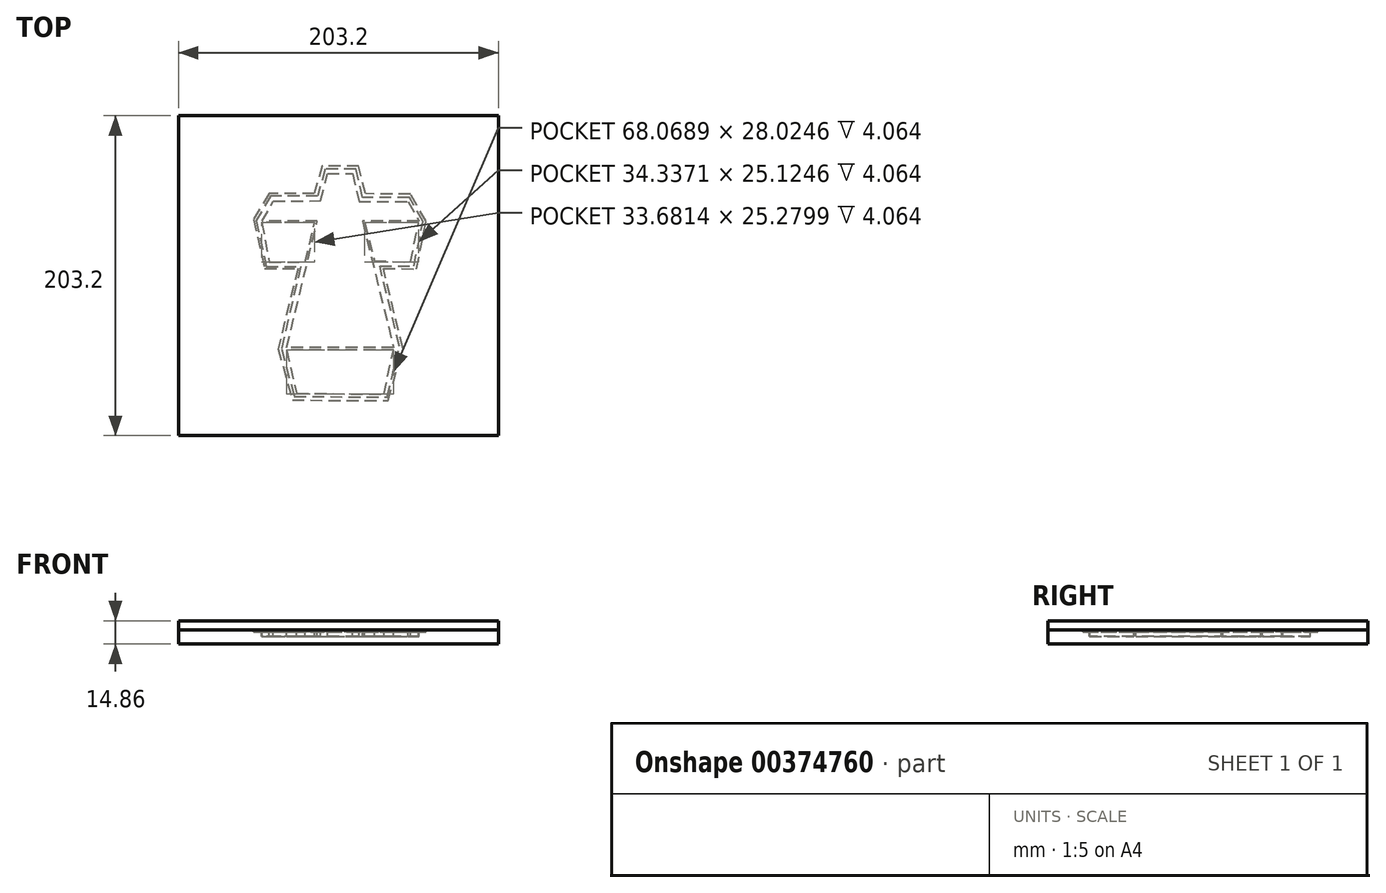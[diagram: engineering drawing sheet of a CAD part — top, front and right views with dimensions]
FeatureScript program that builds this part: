
annotation { "Feature Type Name" : "Feature", "Feature Type Description" : "" }
export const myFeature = defineFeature(function(context is Context, id is Id, definition is map)
    precondition{}
    {
        {
            var Q0;
            Q0=qCreatedBy(makeId("Top.planeOp"),FACE);
            var sketch = newSketch(context, id + "F0", { "sketchPlane" : qUnion([Q0])});
            skLineSegment(sketch, "E0.bottom", {"start": v(0, 0) * mm, "end": v(101.6, 0) * mm});
            skLineSegment(sketch, "E0.top", {"start": v(0, 101.6) * mm, "end": v(101.6, 101.6) * mm});
            skLineSegment(sketch, "E0.left", {"start": v(0, 0) * mm, "end": v(0, 101.6) * mm});
            skLineSegment(sketch, "E0.right", {"start": v(101.6, 0) * mm, "end": v(101.6, 101.6) * mm});
            skSolve(sketch);
        }
        {
            var Q0;
            Q0 = qSketchRegion(id + "F0", true);
            extrude(context, id + "F1", {"entities" : qUnion([Q0]), "depth" : 4.44 * mm});
        }
        {
            var Q0;
            Q0=qCreatedBy(makeId("Top.planeOp"),FACE);
            var sketch = newSketch(context, id + "F2", { "sketchPlane" : qUnion([Q0])});
            skLineSegment(sketch, "E1", {"start": v(33.3, 27.25) * mm, "end": v(67.33, 27.25) * mm});
            skLineSegment(sketch, "E2", {"start": v(67.33, 27.25) * mm, "end": v(64.05, 13.42) * mm});
            skLineSegment(sketch, "E3", {"start": v(64.05, 13.42) * mm, "end": v(36.34, 13.24) * mm});
            skLineSegment(sketch, "E4", {"start": v(36.34, 13.24) * mm, "end": v(33.3, 27.25) * mm});
            skLineSegment(sketch, "E5", {"start": v(33.27, 27.95) * mm, "end": v(67.18, 27.95) * mm});
            skLineSegment(sketch, "E6", {"start": v(67.18, 27.95) * mm, "end": v(57.5, 68.13) * mm});
            skLineSegment(sketch, "E7", {"start": v(57.5, 68.13) * mm, "end": v(74.96, 68.13) * mm});
            skLineSegment(sketch, "E8", {"start": v(74.96, 68.13) * mm, "end": v(71.49, 74.45) * mm});
            skLineSegment(sketch, "E9", {"start": v(71.49, 74.45) * mm, "end": v(56.48, 74.61) * mm});
            skLineSegment(sketch, "E10", {"start": v(56.48, 74.61) * mm, "end": v(54.27, 83.33) * mm});
            skLineSegment(sketch, "E11", {"start": v(54.27, 83.33) * mm, "end": v(46.3, 83.33) * mm});
            skLineSegment(sketch, "E12", {"start": v(46.3, 83.33) * mm, "end": v(44.3, 74.4) * mm});
            skLineSegment(sketch, "E13", {"start": v(44.3, 74.4) * mm, "end": v(28.63, 74.35) * mm});
            skLineSegment(sketch, "E14", {"start": v(28.63, 74.35) * mm, "end": v(25.18, 68.15) * mm});
            skLineSegment(sketch, "E15", {"start": v(25.18, 68.15) * mm, "end": v(43.15, 68.15) * mm});
            skLineSegment(sketch, "E16", {"start": v(43.15, 68.15) * mm, "end": v(33.27, 27.95) * mm});
            skLineSegment(sketch, "E17", {"start": v(27.84, 55.17) * mm, "end": v(25.3, 67.74) * mm});
            skLineSegment(sketch, "E18", {"start": v(25.3, 67.74) * mm, "end": v(42.46, 67.74) * mm});
            skLineSegment(sketch, "E19", {"start": v(42.46, 67.74) * mm, "end": v(39.37, 55.52) * mm});
            skLineSegment(sketch, "E20", {"start": v(39.37, 55.52) * mm, "end": v(27.84, 55.17) * mm});
            skLineSegment(sketch, "E21", {"start": v(61.35, 55.14) * mm, "end": v(58.33, 67.72) * mm});
            skLineSegment(sketch, "E22", {"start": v(58.33, 67.72) * mm, "end": v(75.17, 67.78) * mm});
            skLineSegment(sketch, "E23", {"start": v(75.17, 67.78) * mm, "end": v(72.74, 55.17) * mm});
            skLineSegment(sketch, "E24", {"start": v(72.74, 55.17) * mm, "end": v(61.35, 55.14) * mm});
            skLineSegment(sketch, "E25", {"start": v(31.23, 27.83) * mm, "end": v(37.63, 53.87) * mm});
            skLineSegment(sketch, "E26", {"start": v(37.63, 53.87) * mm, "end": v(26.8, 53.87) * mm});
            skLineSegment(sketch, "E27", {"start": v(26.8, 53.87) * mm, "end": v(23.84, 67.92) * mm});
            skLineSegment(sketch, "E28", {"start": v(23.84, 67.92) * mm, "end": v(28.27, 75.64) * mm});
            skLineSegment(sketch, "E29", {"start": v(28.27, 75.64) * mm, "end": v(43.14, 75.64) * mm});
            skLineSegment(sketch, "E30", {"start": v(43.14, 75.64) * mm, "end": v(45.18, 84.73) * mm});
            skLineSegment(sketch, "E31", {"start": v(45.18, 84.73) * mm, "end": v(55.09, 84.73) * mm});
            skLineSegment(sketch, "E32", {"start": v(55.09, 84.73) * mm, "end": v(57.37, 76.07) * mm});
            skLineSegment(sketch, "E33", {"start": v(57.37, 76.07) * mm, "end": v(72.25, 76.07) * mm});
            skLineSegment(sketch, "E34", {"start": v(72.25, 76.07) * mm, "end": v(76.93, 68.32) * mm});
            skLineSegment(sketch, "E35", {"start": v(76.93, 68.32) * mm, "end": v(73.68, 53.8) * mm});
            skLineSegment(sketch, "E36", {"start": v(73.68, 53.8) * mm, "end": v(62.8, 53.78) * mm});
            skLineSegment(sketch, "E37", {"start": v(62.8, 53.78) * mm, "end": v(68.9, 27.55) * mm});
            skLineSegment(sketch, "E38", {"start": v(68.9, 27.55) * mm, "end": v(64.68, 12.02) * mm});
            skLineSegment(sketch, "E39", {"start": v(64.68, 12.02) * mm, "end": v(35.19, 11.83) * mm});
            skLineSegment(sketch, "E40", {"start": v(35.19, 11.83) * mm, "end": v(31.23, 27.83) * mm});
            skLineSegment(sketch, "E41", {"start": v(34.82, 11.04) * mm, "end": v(30.12, 27.76) * mm});
            skLineSegment(sketch, "E42", {"start": v(30.12, 27.76) * mm, "end": v(36.13, 52.85) * mm});
            skLineSegment(sketch, "E43", {"start": v(36.13, 52.85) * mm, "end": v(25.99, 52.78) * mm});
            skLineSegment(sketch, "E44", {"start": v(25.99, 52.78) * mm, "end": v(22.75, 67.97) * mm});
            skLineSegment(sketch, "E45", {"start": v(22.75, 67.97) * mm, "end": v(27.91, 76.74) * mm});
            skLineSegment(sketch, "E46", {"start": v(27.91, 76.74) * mm, "end": v(42.38, 76.84) * mm});
            skLineSegment(sketch, "E47", {"start": v(42.38, 76.84) * mm, "end": v(44.37, 85.7) * mm});
            skLineSegment(sketch, "E48", {"start": v(44.37, 85.7) * mm, "end": v(55.99, 85.7) * mm});
            skLineSegment(sketch, "E49", {"start": v(55.99, 85.7) * mm, "end": v(58.47, 76.89) * mm});
            skLineSegment(sketch, "E50", {"start": v(58.47, 76.89) * mm, "end": v(72.85, 76.98) * mm});
            skLineSegment(sketch, "E51", {"start": v(72.85, 76.98) * mm, "end": v(77.76, 68.69) * mm});
            skLineSegment(sketch, "E52", {"start": v(77.76, 68.69) * mm, "end": v(74.25, 53.04) * mm});
            skLineSegment(sketch, "E53", {"start": v(74.25, 53.04) * mm, "end": v(63.89, 53.04) * mm});
            skLineSegment(sketch, "E54", {"start": v(63.89, 53.04) * mm, "end": v(69.95, 28.5) * mm});
            skLineSegment(sketch, "E55", {"start": v(69.95, 28.5) * mm, "end": v(65.02, 11.23) * mm});
            skLineSegment(sketch, "E56", {"start": v(65.02, 11.23) * mm, "end": v(34.82, 11.04) * mm});
            skSolve(sketch);
        }
        {
            var Q0;
            Q0=qCreatedBy(makeId("Top.planeOp"),FACE);
            var sketch = newSketch(context, id + "F3", { "sketchPlane" : qUnion([Q0])});
            skLineSegment(sketch, "E57", {"start": v(31.37, 28.38) * mm, "end": v(37.63, 53.87) * mm});
            skLineSegment(sketch, "E58", {"start": v(37.63, 53.87) * mm, "end": v(26.8, 53.87) * mm});
            skLineSegment(sketch, "E59", {"start": v(26.8, 53.87) * mm, "end": v(23.97, 68.09) * mm});
            skLineSegment(sketch, "E60", {"start": v(23.97, 68.09) * mm, "end": v(28.27, 75.64) * mm});
            skLineSegment(sketch, "E61", {"start": v(28.27, 75.64) * mm, "end": v(43.14, 75.64) * mm});
            skLineSegment(sketch, "E62", {"start": v(43.14, 75.64) * mm, "end": v(45.18, 84.73) * mm});
            skLineSegment(sketch, "E63", {"start": v(45.18, 84.73) * mm, "end": v(55.09, 84.73) * mm});
            skLineSegment(sketch, "E64", {"start": v(55.09, 84.73) * mm, "end": v(57.37, 76.07) * mm});
            skLineSegment(sketch, "E65", {"start": v(57.37, 76.07) * mm, "end": v(72.25, 76.07) * mm});
            skLineSegment(sketch, "E66", {"start": v(72.25, 76.07) * mm, "end": v(76.93, 68.32) * mm});
            skLineSegment(sketch, "E67", {"start": v(76.93, 68.32) * mm, "end": v(73.68, 53.8) * mm});
            skLineSegment(sketch, "E68", {"start": v(73.68, 53.8) * mm, "end": v(62.8, 53.78) * mm});
            skLineSegment(sketch, "E69", {"start": v(62.8, 53.78) * mm, "end": v(68.9, 27.55) * mm});
            skLineSegment(sketch, "E70", {"start": v(68.9, 27.55) * mm, "end": v(64.8, 12.46) * mm});
            skLineSegment(sketch, "E71", {"start": v(64.8, 12.46) * mm, "end": v(35.35, 12.28) * mm});
            skLineSegment(sketch, "E72", {"start": v(35.35, 12.28) * mm, "end": v(31.37, 28.38) * mm});
            skLineSegment(sketch, "E73", {"start": v(35.03, 11.11) * mm, "end": v(30.34, 27.77) * mm});
            skLineSegment(sketch, "E74", {"start": v(30.34, 27.77) * mm, "end": v(36.5, 53.05) * mm});
            skLineSegment(sketch, "E75", {"start": v(36.5, 53.05) * mm, "end": v(25.95, 52.98) * mm});
            skLineSegment(sketch, "E76", {"start": v(25.95, 52.98) * mm, "end": v(22.98, 68.1) * mm});
            skLineSegment(sketch, "E77", {"start": v(22.98, 68.1) * mm, "end": v(27.91, 76.74) * mm});
            skLineSegment(sketch, "E78", {"start": v(27.91, 76.74) * mm, "end": v(42.14, 76.83) * mm});
            skLineSegment(sketch, "E79", {"start": v(42.14, 76.83) * mm, "end": v(44.37, 85.7) * mm});
            skLineSegment(sketch, "E80", {"start": v(44.37, 85.7) * mm, "end": v(55.99, 85.7) * mm});
            skLineSegment(sketch, "E81", {"start": v(55.99, 85.7) * mm, "end": v(58.47, 76.89) * mm});
            skLineSegment(sketch, "E82", {"start": v(58.47, 76.89) * mm, "end": v(72.85, 76.98) * mm});
            skLineSegment(sketch, "E83", {"start": v(72.85, 76.98) * mm, "end": v(77.76, 68.69) * mm});
            skLineSegment(sketch, "E84", {"start": v(77.76, 68.69) * mm, "end": v(74.25, 53.04) * mm});
            skLineSegment(sketch, "E85", {"start": v(74.25, 53.04) * mm, "end": v(63.67, 53.04) * mm});
            skLineSegment(sketch, "E86", {"start": v(63.67, 53.04) * mm, "end": v(69.95, 27.61) * mm});
            skLineSegment(sketch, "E87", {"start": v(69.95, 27.61) * mm, "end": v(65.42, 11.3) * mm});
            skLineSegment(sketch, "E88", {"start": v(65.42, 11.3) * mm, "end": v(35.03, 11.11) * mm});
            skPoint(sketch, "E89.end.orphan", {"position": v(27.84, 55.17) * mm});
            skPoint(sketch, "E90.start.orphan", {"position": v(72.74, 55.17) * mm});
            skSolve(sketch);
        }
        {
            var Q0;
            Q0=makeQuery(id+"F2.imprint","IMPRINT",FACE,{"disambiguationData":[TD([[makeQuery(id+"F2.imprint","IMPRINT",EDGE,{"derivedFrom":sQuery(id+"F2.wireOp",EDGE,"E5")}),1.0]])]});
            var Q1;
            Q1=makeQuery(id+"F2.imprint","IMPRINT",FACE,{"disambiguationData":[TD([[makeQuery(id+"F2.imprint","IMPRINT",EDGE,{"derivedFrom":sQuery(id+"F2.wireOp",EDGE,"E1")}),-1.0]])]});
            var Q2;
            Q2=makeQuery(id+"F2.imprint","IMPRINT",FACE,{"disambiguationData":[TD([[makeQuery(id+"F2.imprint","IMPRINT",EDGE,{"derivedFrom":sQuery(id+"F2.wireOp",EDGE,"E17")}),-1.0]])]});
            var Q3;
            Q3=makeQuery(id+"F2.imprint","IMPRINT",FACE,{"disambiguationData":[TD([[makeQuery(id+"F2.imprint","IMPRINT",EDGE,{"derivedFrom":sQuery(id+"F2.wireOp",EDGE,"E21")}),-1.0]])]});
            extrude(context, id + "F4", {"entities" : qUnion([Q0, Q1, Q2, Q3]), "operationType" : NewBodyOperationType.REMOVE, "depth" : 2.03 * mm});
        }
        {
            var Q0;
            Q0 = qSketchRegion(id + "F3", true);
            extrude(context, id + "F5", {"entities" : qUnion([Q0]), "operationType" : NewBodyOperationType.REMOVE, "depth" : 0.5 * mm});
        }
        {
            var Q0;
            Q0=makeQuery(id+"F1.opExtrude","CAP_FACE",FACE,{"disambiguationData":[OSD([sQuery(id+"F0.wireOp",EDGE,"E0.bottom"),sQuery(id+"F0.wireOp",EDGE,"E0.top"),sQuery(id+"F0.wireOp",EDGE,"E0.left"),sQuery(id+"F0.wireOp",EDGE,"E0.right")])],"isStart":false});
            var sketch = newSketch(context, id + "F6", { "sketchPlane" : qUnion([Q0])});
            skLineSegment(sketch, "E91", {"start": v(50.8, 101.6) * mm, "end": v(50.8, 0) * mm});
            skSolve(sketch);
        }
        {
            var Q0;
            Q0=makeQuery(id+"F1.opExtrude","SWEPT_BODY",BODY,{"disambiguationData":[OSD([sQuery(id+"F0.wireOp",EDGE,"E0.bottom"),sQuery(id+"F0.wireOp",EDGE,"E0.top"),sQuery(id+"F0.wireOp",EDGE,"E0.left"),sQuery(id+"F0.wireOp",EDGE,"E0.right")])]});
            var Q1;
            Q1=sQuery(id+"F6.wireOp",EDGE,"E91");
            transform(context, id + "F7", {"entities" : qUnion([Q0]), "transformType" : TransformType.ROTATION, "transformAxis" : qUnion([Q1]), "angle" : 180 * degree, "makeCopy" : false});
        }
        {
            var Q0;
            Q0=makeQuery(id+"F1.opExtrude","SWEPT_BODY",BODY,{"disambiguationData":[OSD([sQuery(id+"F0.wireOp",EDGE,"E0.bottom"),sQuery(id+"F0.wireOp",EDGE,"E0.top"),sQuery(id+"F0.wireOp",EDGE,"E0.left"),sQuery(id+"F0.wireOp",EDGE,"E0.right")])]});
            var Q1;
            Q1=qCreatedBy(makeId("Origin.pointOp"),VERTEX);
            transform(context, id + "F8", {"entities" : qUnion([Q0]), "transformType" : TransformType.SCALE_UNIFORMLY, "scale" : 2, "scalePoint" : qUnion([Q1]), "makeCopy" : false});
        }
        {
            var Q0;
            {var subQ0=sQuery(id+"F0.wireOp",EDGE,"E0.bottom");var subQ1=sQuery(id+"F0.wireOp",EDGE,"E0.right");var subQ2=sQuery(id+"F0.wireOp",EDGE,"E0.top");var subQ3=sQuery(id+"F0.wireOp",EDGE,"E0.left");Q0=makeQuery(id+"F5.boolean.opBoolean","SPLIT",FACE,{"disambiguationData":[TD([makeQuery(id+"F1.opExtrude","SWEPT_FACE",FACE,{"disambiguationData":[OSD([subQ0])]})])],"derivedFrom":makeQuery(id+"F1.opExtrude","CAP_FACE",FACE,{"disambiguationData":[OSD([subQ0,subQ2,subQ3,subQ1])],"isStart":true})});}
            var sketch = newSketch(context, id + "F9", { "sketchPlane" : qUnion([Q0])});
            skLineSegment(sketch, "E92.bottom", {"start": v(0, 0) * mm, "end": v(203.2, 0) * mm});
            skLineSegment(sketch, "E92.top", {"start": v(0, 203.2) * mm, "end": v(203.2, 203.2) * mm});
            skLineSegment(sketch, "E92.left", {"start": v(0, 0) * mm, "end": v(0, 203.2) * mm});
            skLineSegment(sketch, "E92.right", {"start": v(203.2, 0) * mm, "end": v(203.2, 203.2) * mm});
            skSolve(sketch);
        }
        {
            var Q0;
            Q0 = qSketchRegion(id + "F9", true);
            var Q1;
            Q1=makeQuery(id+"F1.opExtrude","CAP_FACE",FACE,{"disambiguationData":[OSD([sQuery(id+"F0.wireOp",EDGE,"E0.bottom"),sQuery(id+"F0.wireOp",EDGE,"E0.top"),sQuery(id+"F0.wireOp",EDGE,"E0.left"),sQuery(id+"F0.wireOp",EDGE,"E0.right")])],"isStart":false});
            extrude(context, id + "F10", {"entities" : qUnion([Q0]), "endBound" : BoundingType.UP_TO_SURFACE, "oppositeDirection" : true, "endBoundEntityFace" : qUnion([Q1]), "depth" : 25.4 * mm});
        }
        {
            var Q0;
            {var subQ0=sQuery(id+"F0.wireOp",EDGE,"E0.bottom");var subQ1=sQuery(id+"F0.wireOp",EDGE,"E0.right");var subQ2=sQuery(id+"F0.wireOp",EDGE,"E0.top");var subQ3=sQuery(id+"F0.wireOp",EDGE,"E0.left");Q0=makeQuery(id+"F5.boolean.opBoolean","SPLIT",FACE,{"disambiguationData":[TD([makeQuery(id+"F1.opExtrude","SWEPT_FACE",FACE,{"disambiguationData":[OSD([subQ0])]})])],"derivedFrom":makeQuery(id+"F1.opExtrude","CAP_FACE",FACE,{"disambiguationData":[OSD([subQ0,subQ2,subQ3,subQ1])],"isStart":true})});}
            var sketch = newSketch(context, id + "F11", { "sketchPlane" : qUnion([Q0])});
            skLineSegment(sketch, "E93.bottom", {"start": v(0, 0) * mm, "end": v(203.2, 0) * mm});
            skLineSegment(sketch, "E93.top", {"start": v(0, 203.2) * mm, "end": v(203.2, 203.2) * mm});
            skLineSegment(sketch, "E93.left", {"start": v(0, 0) * mm, "end": v(0, 203.2) * mm});
            skLineSegment(sketch, "E93.right", {"start": v(203.2, 0) * mm, "end": v(203.2, 203.2) * mm});
            skSolve(sketch);
        }
        {
            var Q0;
            Q0 = qSketchRegion(id + "F11", true);
            extrude(context, id + "F12", {"entities" : qUnion([Q0]), "depth" : 5.97 * mm});
        }
    });
